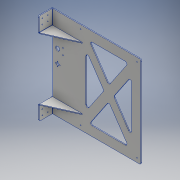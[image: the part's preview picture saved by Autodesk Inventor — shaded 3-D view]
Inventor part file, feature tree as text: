
AUTODESK INVENTOR PART (.ipt)
format: ipt  version: 2019 (Build 230136000, 136)  size: 396,288 bytes
history: native  units: mm
features: other x9, sketch x8, sheet_metal_op x6, mirror x1, hole x1, chamfer x1
ambient origin geometry x8: Origin, YZ Plane, XZ Plane, XY Plane, X Axis, Y Axis, Z Axis, Center Point
bodies: Solid1 (feature_tree)
feature tree (26):
  sheet_metal_op  "Contour Flange1"
  mirror  "Mirror1"
  hole  "Hole1"  [1 undecoded]
  sheet_metal_op  "Flange2"
  chamfer  "Corner Round3"
  sketch  "Sketch1"  dims[d0=50.0mm d1=330.0mm]
  other  "Plate1"
  sheet_metal_op  "Bend1"
  sheet_metal_op  "Corner1"
  sketch  "Sketch2"  dims[d2=0.2mm]
  sketch  "Sketch3"  dims[d3=0.2mm]
  sketch  "Sketch6"  dims[d4=0.2mm]
  sketch  "Sketch7"  dims[d5=0.8mm]
  sketch  "Sketch9"  dims[d6=340.0mm]
  other  "Plate3"
  sheet_metal_op  "Bend3"
  sheet_metal_op  "Corner3"
  sketch  "Sketch10"  dims[d7=0.8mm]
  sketch  "Sketch11"  dims[d8=3.0mm d9=12.0mm d10=0.2mm d11=0.8mm d12=20.0mm d13=12.5mm d14=13.5mm d15=3.2mm d16=3.0mm d17=0.0mm d19=15.0mm d20=15.0mm d21=210.0mm d22=310.0mm d23=3.0mm d24=3.2mm d25=6.0mm d26=4.0mm d27=2.0mm d28=90.0deg d29=3.0mm d30=20.594885mm d49=19.5mm d50=10.2mm d51=3.0mm d52=0.0mm d54=2.5mm d55=16.0mm d56=170.0mm d57=3.0mm d58=15.0mm d59=4.0mm d60=50.0mm d61=20.0mm d62=3.0mm d63=0.0mm d64=235.0mm d65=70.0mm d66=5.0mm d67=0.0mm d78=0.2mm d79=0.2mm d80=0.2mm d81=0.8mm d82=115.0mm d83=90.0deg d84=0.8mm d85=12.0mm d86=0.2mm d87=0.8mm d88=3.0mm d89=0.0mm d90=6.0mm d92=20.0mm d93=15.0mm d94=20.0mm d95=15.0mm d96=3.0mm d97=0.0mm]
  other  "Cut1"
  other  "Cut3"
  other  "Cut4"
  other  "Cut5"
  other  "Cut6"
  other  "Cut7"
  other  "Definition1"
note: 1 required parameter value undecoded (feature->parameter linkage not recoverable at this tier; creation-order binding heuristic only, values carry confidence <= 0.55)
